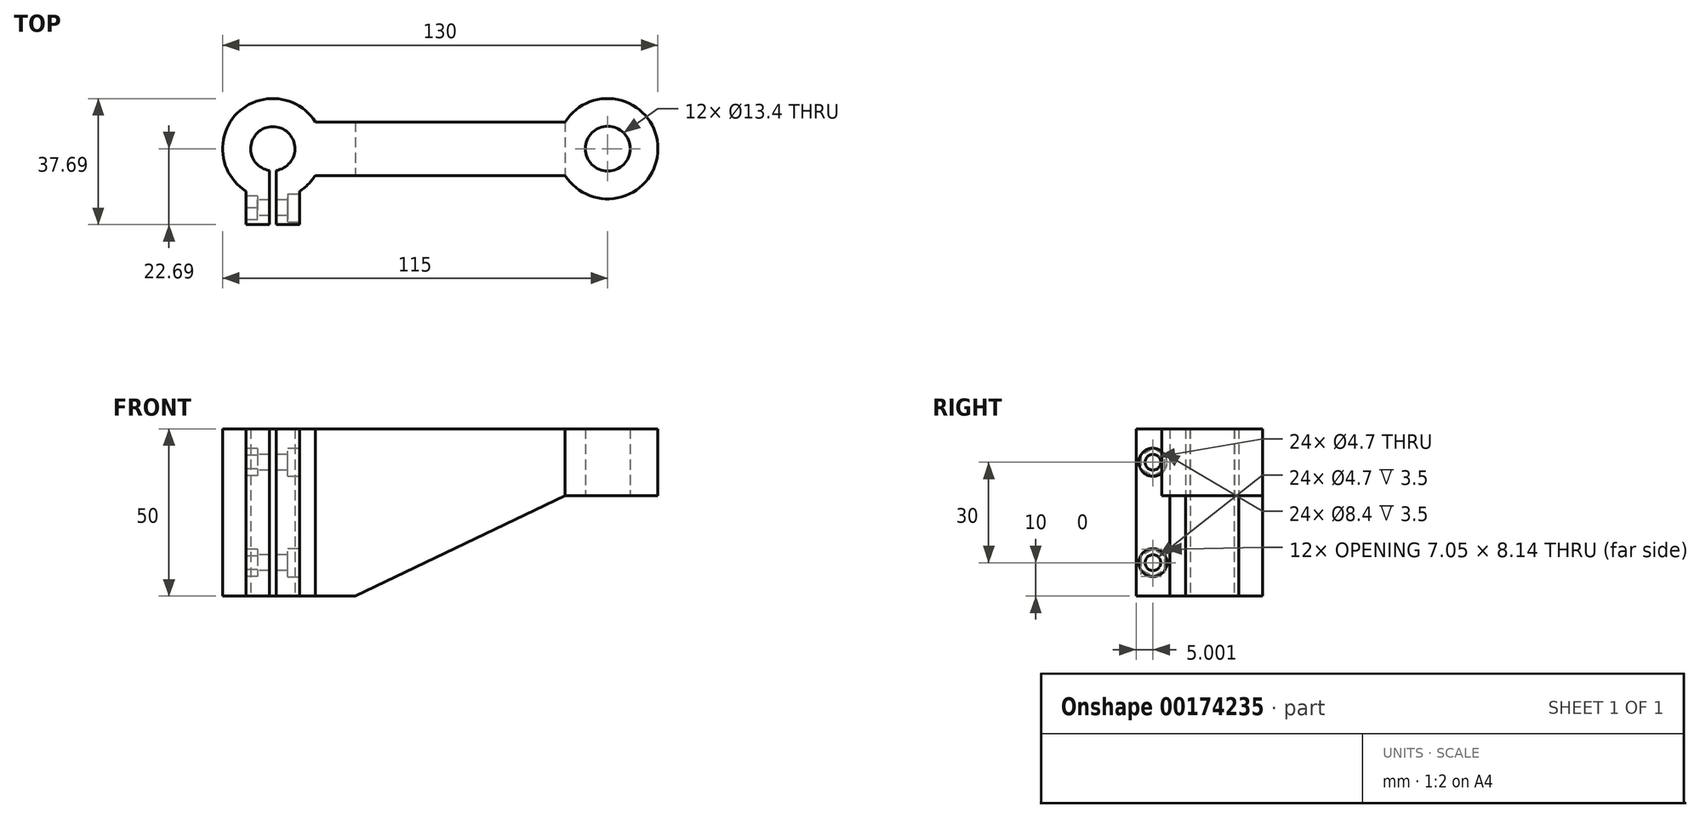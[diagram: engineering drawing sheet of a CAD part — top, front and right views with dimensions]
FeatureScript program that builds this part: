
annotation { "Feature Type Name" : "Feature", "Feature Type Description" : "" }
export const myFeature = defineFeature(function(context is Context, id is Id, definition is map)
    precondition{}
    {
        {
            var Q0;
            Q0=qCreatedBy(makeId("Top.planeOp"),FACE);
            var sketch = newSketch(context, id + "F0", { "sketchPlane" : qUnion([Q0])});
            skArc(sketch, "E0", {"start": v(-42, -12.69) * mm, "mid": v(-39.4, -10.6) * mm, "end": v(-37.31, -8) * mm});
            skArc(sketch, "E1", {"start": v(37.31, -8) * mm, "mid": v(65, 0) * mm, "end": v(37.31, 8) * mm});
            skLineSegment(sketch, "E2.bottom", {"start": v(-37.31, 8) * mm, "end": v(37.31, 8) * mm});
            skLineSegment(sketch, "E2.top", {"start": v(-37.31, -8) * mm, "end": v(37.31, -8) * mm});
            skLineSegment(sketch, "E3.top", {"start": v(-58, -22.69) * mm, "end": v(-51, -22.69) * mm});
            skLineSegment(sketch, "E3.left", {"start": v(-58, -12.69) * mm, "end": v(-58, -22.69) * mm});
            skLineSegment(sketch, "E3.right", {"start": v(-42, -12.69) * mm, "end": v(-42, -22.69) * mm});
            skLineSegment(sketch, "E4", {"start": v(-50, 47.51) * mm, "end": v(-50, -34.4) * mm, "construction": true});
            skArc(sketch, "E5", {"start": v(-49, -6.52) * mm, "mid": v(-50, 6.6) * mm, "end": v(-51, -6.52) * mm});
            skPoint(sketch, "E6.orphan", {"position": v(-37.14, 8) * mm});
            skPoint(sketch, "E7.orphan", {"position": v(-37.14, -8) * mm});
            skArc(sketch, "E8.trimOffspring", {"start": v(-37.31, 8) * mm, "mid": v(-60.6, 10.6) * mm, "end": v(-58, -12.69) * mm});
            skCircle(sketch, "E9", {"center": v(50, 0) * mm, "radius": 6.7 * mm});
            skLineSegment(sketch, "E10.left", {"start": v(-51, -6.52) * mm, "end": v(-51, -22.69) * mm});
            skLineSegment(sketch, "E10.right", {"start": v(-49, -6.52) * mm, "end": v(-49, -22.69) * mm});
            skLineSegment(sketch, "E11.trimOffspring", {"start": v(-49, -22.69) * mm, "end": v(-42, -22.69) * mm});
            skSolve(sketch);
        }
        {
            var Q0;
            Q0 = qSketchRegion(id + "F0", true);
            extrude(context, id + "F1", {"entities" : qUnion([Q0]), "depth" : 50 * mm});
        }
        {
            var Q0;
            Q0=makeQuery(id+"F1.opExtrude","SWEPT_FACE",FACE,{"disambiguationData":[OSD([sQuery(id+"F0.wireOp",EDGE,"E2.top")])]});
            cPlane(context, id + "F2", {"entities" : qUnion([Q0]), "cplaneType" : CPlaneType.OFFSET, "offset" : 15 * mm, "width" : 150 * mm, "height" : 150 * mm});
        }
        {
            var Q0;
            Q0=qCreatedBy(id+"F2.planeOp",FACE);
            var sketch = newSketch(context, id + "F3", { "sketchPlane" : qUnion([Q0])});
            skLineSegment(sketch, "E12", {"start": v(-25.31, 0) * mm, "end": v(37.31, 30) * mm});
            skLineSegment(sketch, "E13", {"start": v(37.31, 30) * mm, "end": v(77.77, 30) * mm});
            skLineSegment(sketch, "E14", {"start": v(77.77, 30) * mm, "end": v(77.77, 0) * mm});
            skLineSegment(sketch, "E15", {"start": v(77.77, 0) * mm, "end": v(-25.31, 0) * mm});
            skSolve(sketch);
        }
        {
            var Q0;
            Q0 = qSketchRegion(id + "F3", true);
            extrude(context, id + "F4", {"entities" : qUnion([Q0]), "operationType" : NewBodyOperationType.REMOVE, "endBound" : BoundingType.THROUGH_ALL, "oppositeDirection" : true, "depth" : 50 * mm});
        }
        {
            var Q0;
            Q0=makeQuery(id+"F1.opExtrude","SWEPT_FACE",FACE,{"disambiguationData":[OSD([sQuery(id+"F0.wireOp",EDGE,"E3.left")])]});
            var sketch = newSketch(context, id + "F5", { "sketchPlane" : qUnion([Q0])});
            skLineSegment(sketch, "E16", {"start": v(17.69, 55.14) * mm, "end": v(17.69, -3.78) * mm, "construction": true});
            skCircle(sketch, "E17", {"center": v(17.69, 40) * mm, "radius": 2.35 * mm});
            skCircle(sketch, "E18", {"center": v(17.69, 10) * mm, "radius": 2.35 * mm});
            skSolve(sketch);
        }
        {
            var Q0;
            Q0 = qSketchRegion(id + "F5", true);
            extrude(context, id + "F6", {"entities" : qUnion([Q0]), "operationType" : NewBodyOperationType.REMOVE, "oppositeDirection" : true, "depth" : 20 * mm});
        }
        {
            var Q0;
            Q0=makeQuery(id+"F1.opExtrude","SWEPT_FACE",FACE,{"disambiguationData":[OSD([sQuery(id+"F0.wireOp",EDGE,"E3.left")])]});
            var sketch = newSketch(context, id + "F7", { "sketchPlane" : qUnion([Q0])});
            skCircle(sketch, "E19.cCircle", {"center": v(17.69, 40) * mm, "radius": 3.53 * mm, "construction": true});
            skLineSegment(sketch, "E19.0", {"start": v(21.21, 37.96) * mm, "end": v(17.69, 35.93) * mm});
            skLineSegment(sketch, "E19.1", {"start": v(17.69, 35.93) * mm, "end": v(14.16, 37.96) * mm});
            skLineSegment(sketch, "E19.2", {"start": v(14.16, 37.96) * mm, "end": v(14.16, 42.04) * mm});
            skLineSegment(sketch, "E19.3", {"start": v(14.16, 42.04) * mm, "end": v(17.69, 44.07) * mm});
            skLineSegment(sketch, "E19.4", {"start": v(17.69, 44.07) * mm, "end": v(21.21, 42.04) * mm});
            skLineSegment(sketch, "E19.5", {"start": v(21.21, 42.04) * mm, "end": v(21.21, 37.96) * mm});
            skPoint(sketch, "E19.0.midPoint", {"position": v(19.45, 36.95) * mm});
            skCircle(sketch, "E20.cCircle", {"center": v(17.69, 10) * mm, "radius": 3.53 * mm, "construction": true});
            skLineSegment(sketch, "E20.0", {"start": v(21.21, 7.96) * mm, "end": v(17.69, 5.93) * mm});
            skLineSegment(sketch, "E20.1", {"start": v(17.69, 5.93) * mm, "end": v(14.16, 7.96) * mm});
            skLineSegment(sketch, "E20.2", {"start": v(14.16, 7.96) * mm, "end": v(14.16, 12.04) * mm});
            skLineSegment(sketch, "E20.3", {"start": v(14.16, 12.04) * mm, "end": v(17.69, 14.07) * mm});
            skLineSegment(sketch, "E20.4", {"start": v(17.69, 14.07) * mm, "end": v(21.21, 12.04) * mm});
            skLineSegment(sketch, "E20.5", {"start": v(21.21, 12.04) * mm, "end": v(21.21, 7.96) * mm});
            skPoint(sketch, "E20.0.midPoint", {"position": v(19.45, 6.95) * mm});
            skSolve(sketch);
        }
        {
            var Q0;
            Q0 = qSketchRegion(id + "F7", true);
            extrude(context, id + "F8", {"entities" : qUnion([Q0]), "operationType" : NewBodyOperationType.REMOVE, "oppositeDirection" : true, "depth" : 3.5 * mm});
        }
        {
            var Q0;
            Q0=makeQuery(id+"F1.opExtrude","SWEPT_FACE",FACE,{"disambiguationData":[OSD([sQuery(id+"F0.wireOp",EDGE,"E3.right")])]});
            var sketch = newSketch(context, id + "F9", { "sketchPlane" : qUnion([Q0])});
            skCircle(sketch, "E21", {"center": v(-17.69, 40) * mm, "radius": 4.2 * mm});
            skCircle(sketch, "E22", {"center": v(-17.69, 10) * mm, "radius": 4.2 * mm});
            skSolve(sketch);
        }
        {
            var Q0;
            Q0 = qSketchRegion(id + "F9", true);
            extrude(context, id + "F10", {"entities" : qUnion([Q0]), "operationType" : NewBodyOperationType.REMOVE, "oppositeDirection" : true, "depth" : 3.5 * mm});
        }
    });
